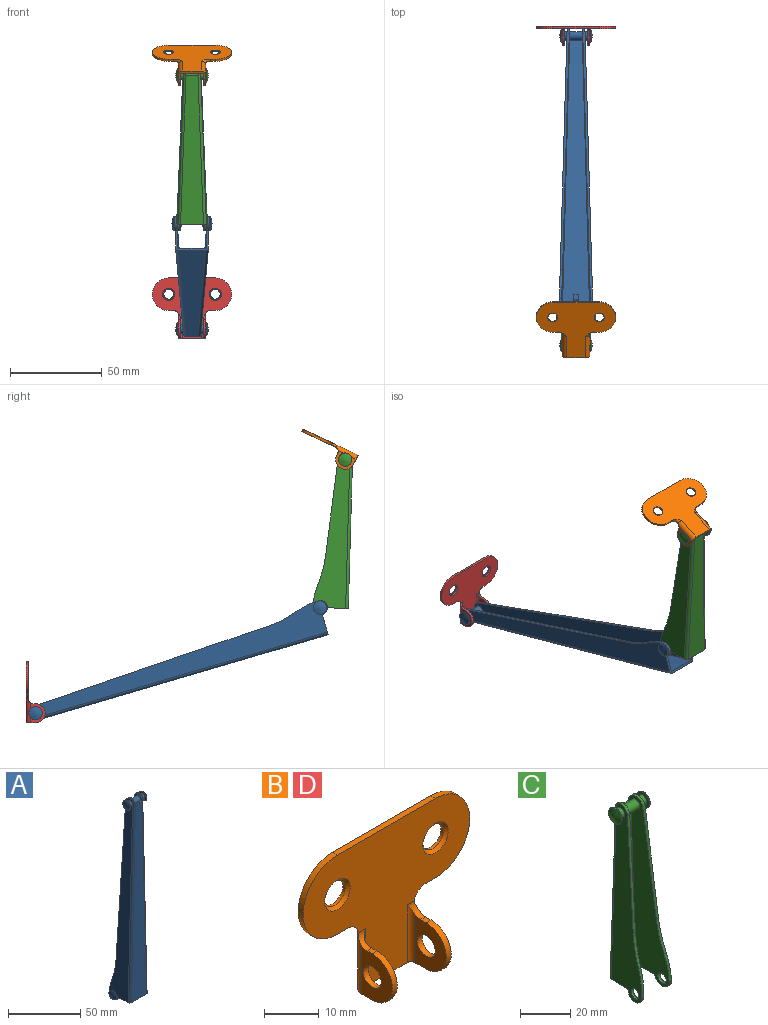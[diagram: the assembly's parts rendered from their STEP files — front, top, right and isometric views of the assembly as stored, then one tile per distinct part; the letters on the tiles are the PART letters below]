
ASSEMBLY  parts=4 mates=4
PART A: 52 faces, bbox 22.4x21.2x174.7 mm
  f0: cylinder r=1.52mm len=168.21mm, axis (0.03,0,1), area 390.4mm2, adj f3,f5,f12,f14,f15,f17
  f1: cylinder r=1.52mm len=168.21mm, axis (0.03,0,-1), area 390.5mm2, adj f4,f5,f12,f13,f15,f16
  f2: plane 165.1x15.3mm, normal (0,1,0), area 1825.2mm2, adj f5,f15,f16,f17,f20,f21,f25,f26
  f3: cylinder r=3.94mm len=7.86mm, axis (-1,0,0), area 12.5mm2, adj f0,f10,f14,f17
  f4: cylinder r=3.94mm len=7.86mm, axis (-1,0,0), area 12.5mm2, adj f1,f11,f13,f16
  f5: plane 18.57x11.45mm, normal (0,0,-1), area 47.5mm2, adj f0,f1,f2,f6,f7,f12,f13,f14
  f6: cylinder r=3.94mm len=7.87mm, axis (-1,0,0), area 15.7mm2, adj f5,f8,f14,f17
  f7: cylinder r=3.94mm len=7.87mm, axis (-1,0,0), area 15.7mm2, adj f5,f9,f13,f16
  f8: cylinder r=35.37mm len=12.06mm, axis (-1,0,0), area 15.6mm2, adj f6,f14,f17,f19
  f9: cylinder r=35.37mm len=12.06mm, axis (-1,0,0), area 15.6mm2, adj f7,f13,f16,f18
  f10: plane 135.82x5.87mm, normal (0,1,0.04), area 172.8mm2, adj f3,f14,f17,f19
  f11: plane 135.82x5.87mm, normal (0,1,0.04), area 172.8mm2, adj f4,f13,f16,f18
  f12: plane 165.1x14.81mm, normal (0,-1,0), area 1749.8mm2, adj f0,f1,f5,f15
  f13: plane 173.37x18.23mm, normal (1,-0.03,0.03), area 1722.3mm2, adj f1,f4,f5,f7,f9,f11,f18,f30
  f14: plane 173.33x18.18mm, normal (-1,-0.03,0.03), area 1722.3mm2, adj f0,f3,f5,f6,f8,f10,f19,f32
  f15: plane 6.88x1.27mm, normal (0,0,1), area 8.7mm2, adj f0,f1,f2,f12,f16,f17
  f16: plane 173.26x19.58mm, normal (-1,0.03,-0.03), area 1758.6mm2, adj f1,f2,f4,f5,f7,f9,f11,f15
  f17: plane 173.37x19.69mm, normal (1,0.03,-0.03), area 1758.6mm2, adj f0,f2,f3,f5,f6,f8,f10,f15
  f18: cylinder r=58.42mm len=17.39mm, axis (-1,0,0), area 22.6mm2, adj f9,f11,f13,f16
  f19: cylinder r=58.42mm len=17.39mm, axis (-1,0,0), area 22.6mm2, adj f8,f10,f14,f17
  f20: plane 2.54x1.14mm, normal (0,-0.71,0.71), area 4.1mm2, adj f2,f24,f25,f26
  f21: plane 2.67x2.67mm, normal (0,0.71,-0.71), area 9.6mm2, adj f2,f22,f25,f26
  f22: plane 3.17x2.54mm, normal (0,1,0), area 8.1mm2, adj f21,f23,f25,f26
  f23: plane 2.54x1.52mm, normal (0,0,1), area 3.9mm2, adj f22,f24,f25,f26
  f24: plane 2.54x2.54mm, normal (0,-1,0), area 6.5mm2, adj f20,f23,f25,f26
  f25: plane 5.84x2.67mm, normal (1,0,0), area 8.5mm2, adj f2,f20,f21,f22,f23,f24
  f26: plane 5.84x2.67mm, normal (-1,0,0), area 8.5mm2, adj f2,f20,f21,f22,f23,f24
  f27: bspline ~7.55x7.44mm, area 43.1mm2, adj f28
  f28: cylinder r=3.64mm len=7.29mm, axis (-1,0,0), area 11.6mm2, adj f27,f29
  f29: plane 7.29x7.29mm, normal (-1,0,0), area 25mm2, adj f28,f30
  f30: cylinder r=2.31mm len=4.62mm, axis (-1,0,0), area 39.5mm2, adj f13,f29
  f31: cylinder r=2.31mm len=7.06mm, axis (-1,0,0), area 101.1mm2, adj f16,f17
  f32: cylinder r=2.31mm len=4.62mm, axis (-1,0,0), area 42.1mm2, adj f14,f33
  f33: plane 7.29x7.29mm, normal (1,0,0), area 25mm2, adj f32,f34
  f34: cylinder r=3.64mm len=7.29mm, axis (1,0,0), area 11.6mm2, adj f33,f35
  f35: bspline ~7.55x7.44mm, area 43.1mm2, adj f34
  f36: bspline ~7.55x7.45mm, area 43.1mm2, adj f37
  f37: cylinder r=3.64mm len=7.29mm, axis (-1,0,0), area 11.6mm2, adj f36,f38
  f38: plane 7.29x7.29mm, normal (-1,0,0), area 25mm2, adj f37,f39
  f39: cylinder r=2.31mm len=4.62mm, axis (-1,0,0), area 3.7mm2, adj f13,f38
  f40: cylinder r=2.31mm len=4.62mm, axis (-1,0,0), area 15.8mm2, adj f16,f41
  f41: plane 7.75x7.75mm, normal (1,-0.03,-0.04), area 24.9mm2, adj f40,f42
  f42: extruded ~7.3x7.29mm, area 11.6mm2, adj f41,f43
  f43: bspline ~10.59x10.59mm, area 43.1mm2, adj f42
  f44: bspline ~7.55x7.45mm, area 43.1mm2, adj f45
  f45: cylinder r=3.64mm len=7.29mm, axis (1,0,0), area 11.6mm2, adj f44,f46
  f46: plane 7.29x7.29mm, normal (1,0,0), area 25mm2, adj f45,f47
  f47: cylinder r=2.31mm len=4.62mm, axis (1,0,0), area 3.7mm2, adj f14,f46
  f48: cylinder r=2.31mm len=4.62mm, axis (1,0,0), area 14.4mm2, adj f17,f49
  f49: plane 7.75x7.75mm, normal (-1,-0.03,-0.04), area 24.9mm2, adj f48,f50
  f50: extruded ~7.3x7.29mm, area 11.6mm2, adj f49,f51
  f51: bspline ~10.59x10.59mm, area 43.1mm2, adj f50
PART B: 30 faces, bbox 43.3x15.4x33.3 mm
  f0: plane 15.24x5.21mm, normal (0,0,-1), area 27mm2, adj f1,f2,f7,f11,f12,f15,f16,f17
  f1: cylinder r=5.21mm len=10.41mm, axis (-1,0,0), area 20.8mm2, adj f0,f3,f15,f20
  f2: cylinder r=5.21mm len=10.41mm, axis (-1,0,0), area 20.8mm2, adj f0,f4,f7,f23
  f3: plane 1.4x1.27mm, normal (0,0,1), area 1.8mm2, adj f1,f5,f15,f20
  f4: plane 1.4x1.27mm, normal (0,0,1), area 1.8mm2, adj f2,f6,f7,f23
  f5: cylinder r=2.54mm len=2.54mm, axis (1,0,0), area 5.5mm2, adj f3,f12,f15,f17,f19,f20,f21
  f6: cylinder r=2.54mm len=2.54mm, axis (1,0,0), area 5.5mm2, adj f4,f7,f12,f16,f18,f22,f23
  f7: plane 10.75x7.87mm, normal (-1,0,0), area 53.7mm2, adj f0,f2,f4,f6,f16,f28
  f8: plane 3.22x1.27mm, normal (0,0,-1), area 3.7mm2, adj f9,f11,f12,f18
  f9: cylinder r=8.89mm len=17.78mm, axis (0,1,0), area 35.5mm2, adj f8,f10,f11,f12
  f10: plane 25.4x1.27mm, normal (0,0,1), area 32.3mm2, adj f9,f11,f12,f14
  f11: plane 43.18x33.15mm, normal (0,1,0), area 819.1mm2, adj f0,f8,f9,f10,f13,f14,f16,f17
  f12: plane 43.3x33.26mm, normal (0,-1,0), area 807.8mm2, adj f0,f5,f6,f8,f9,f10,f13,f14
  f13: plane 3.22x1.27mm, normal (0,0,-1), area 3.7mm2, adj f11,f12,f14,f19
  f14: cylinder r=8.89mm len=17.78mm, axis (0,1,0), area 35.5mm2, adj f10,f11,f12,f13
  f15: plane 10.75x7.87mm, normal (1,0,0), area 53.7mm2, adj f0,f1,f3,f5,f17,f29
  f16: cylinder r=2.54mm len=12.83mm, axis (0,0,-1), area 49.3mm2, adj f0,f6,f7,f11,f18
  f17: cylinder r=2.54mm len=12.83mm, axis (0,0,1), area 49.3mm2, adj f0,f5,f11,f15,f19
  f18: torus R=5.08mm, axis (0,0,-1), area 6.9mm2, adj f6,f8,f11,f12,f16
  f19: torus R=5.08mm, axis (0,0,-1), area 6.9mm2, adj f5,f11,f12,f13,f17
  f20: plane 10.92x8.13mm, normal (-1,0,0), area 56.5mm2, adj f0,f1,f3,f5,f21,f29
  f21: cylinder r=1.02mm len=12.95mm, axis (0,0,-1), area 19.1mm2, adj f0,f5,f12,f20
  f22: cylinder r=1.02mm len=12.95mm, axis (0,0,-1), area 19.1mm2, adj f0,f6,f12,f23
  f23: plane 10.92x8.13mm, normal (1,0,0), area 56.5mm2, adj f0,f2,f4,f6,f22,f28
  f24: cylinder r=2.67mm len=5.33mm, axis (0,-1,0), area 10.6mm2, adj f11,f27
  f25: cylinder r=2.67mm len=5.33mm, axis (0,-1,0), area 10.6mm2, adj f11,f26
  f26: cone r=3.3mm half-angle=45deg, axis (0,-1,0), area 16.8mm2, adj f12,f25
  f27: cone r=3.3mm half-angle=45deg, axis (0,-1,0), area 16.8mm2, adj f12,f24
  f28: cylinder r=2.31mm len=4.62mm, axis (1,0,0), area 18.4mm2, adj f7,f23
  f29: cylinder r=2.31mm len=4.62mm, axis (1,0,0), area 18.4mm2, adj f15,f20
PART C: 38 faces, bbox 18.3x19.8x89.4 mm
  f0: cylinder r=2.31mm len=4.62mm, axis (-1,0,0), area 41.7mm2, adj f1,f18
  f1: plane 7.29x7.29mm, normal (1,0,0), area 25mm2, adj f0,f2
  f2: cylinder r=3.64mm len=7.29mm, axis (1,0,0), area 11.6mm2, adj f1,f3
  f3: bspline ~7.55x7.44mm, area 43.1mm2, adj f2
  f4: cylinder r=1.52mm len=84.15mm, axis (-0.04,0,-1), area 193.7mm2, adj f9,f14,f15,f18,f19,f21
  f5: cylinder r=1.52mm len=84.15mm, axis (-0.04,0,1), area 193.7mm2, adj f11,f14,f15,f16,f19,f20
  f6: plane 81.03x13mm, normal (0,-1,0), area 803.3mm2, adj f14,f19,f20,f21,f29,f30,f31,f32
  f7: cylinder r=35.37mm len=12.81mm, axis (-1,0,0), area 16.7mm2, adj f8,f18,f21,f23
  f8: cylinder r=3.94mm len=7.87mm, axis (-1,0,0), area 15.7mm2, adj f7,f14,f18,f21
  f9: cylinder r=3.94mm len=7.84mm, axis (-1,0,0), area 12mm2, adj f4,f10,f18,f21
  f10: plane 53.31x5.38mm, normal (0,-0.99,0.1), area 68.1mm2, adj f9,f18,f21,f23
  f11: plane 89.37x18.31mm, normal (1,0.03,0.04), area 915mm2, adj f5,f12,f13,f14,f16,f17,f22,f25
  f12: cylinder r=35.37mm len=12.81mm, axis (-1,0,0), area 16.7mm2, adj f11,f13,f20,f22
  f13: cylinder r=3.94mm len=7.87mm, axis (-1,0,0), area 15.7mm2, adj f11,f12,f14,f20
  f14: plane 16.27x11.45mm, normal (0,0,-1), area 44.6mm2, adj f4,f5,f6,f8,f11,f13,f15,f18
  f15: plane 81.03x12.51mm, normal (0,1,0), area 769.1mm2, adj f4,f5,f14,f19
  f16: cylinder r=3.94mm len=7.84mm, axis (-1,0,0), area 12mm2, adj f5,f11,f17,f20
  f17: plane 53.31x5.38mm, normal (0,-0.99,0.1), area 68.1mm2, adj f11,f16,f20,f22
  f18: plane 89.37x18.31mm, normal (-1,0.03,0.04), area 915mm2, adj f0,f4,f7,f8,f9,f10,f14,f23
  f19: plane 6.97x1.28mm, normal (0,0,1), area 8.8mm2, adj f4,f5,f6,f15,f20,f21
  f20: plane 89.37x19.76mm, normal (-1,-0.03,-0.04), area 934.5mm2, adj f5,f6,f12,f13,f14,f16,f17,f19
  f21: plane 89.37x19.76mm, normal (1,-0.03,-0.04), area 934.5mm2, adj f4,f6,f7,f8,f9,f10,f14,f19
  f22: cylinder r=58.42mm len=15.3mm, axis (-1,0,0), area 20.1mm2, adj f11,f12,f17,f20
  f23: cylinder r=58.42mm len=15.3mm, axis (-1,0,0), area 20.1mm2, adj f7,f10,f18,f21
  f24: cylinder r=2.31mm len=4.62mm, axis (1,0,0), area 18.5mm2, adj f18,f21
  f25: cylinder r=2.31mm len=4.62mm, axis (1,0,0), area 18.5mm2, adj f11,f20
  f26: plane 2.54x2.54mm, normal (0,1,0), area 6.5mm2, adj f27,f30,f31,f32
  f27: plane 2.54x1.52mm, normal (0,0,1), area 3.9mm2, adj f26,f28,f31,f32
  f28: plane 3.17x2.54mm, normal (0,-1,0), area 8.1mm2, adj f27,f29,f31,f32
  f29: plane 2.67x2.67mm, normal (0,-0.71,-0.71), area 9.6mm2, adj f6,f28,f31,f32
  f30: plane 2.54x1.14mm, normal (0,0.71,0.71), area 4.1mm2, adj f6,f26,f31,f32
  f31: plane 5.84x2.67mm, normal (1,0,0), area 8.5mm2, adj f6,f26,f27,f28,f29,f30
  f32: plane 5.84x2.67mm, normal (-1,0,0), area 8.5mm2, adj f6,f26,f27,f28,f29,f30
  f33: cylinder r=2.31mm len=7.15mm, axis (-1,0,0), area 102.2mm2, adj f20,f21
  f34: bspline ~7.55x7.44mm, area 43.1mm2, adj f35
  f35: cylinder r=3.64mm len=7.29mm, axis (-1,0,0), area 11.6mm2, adj f34,f36
  f36: plane 7.29x7.29mm, normal (-1,0,0), area 25mm2, adj f35,f37
  f37: cylinder r=2.31mm len=4.62mm, axis (-1,0,0), area 38.5mm2, adj f11,f36
PART D: same geometry as B
PLACE A rot(axis=(0,-0.8,-0.6),180deg) t=(0,-160.37,41.77)mm
PLACE B rot(axis=(0,-0.54,-0.84),180deg) t=(0,-242.59,77.69)mm
PLACE C rot(axis=(0,0.01,-1),180deg) t=(0,-160.37,41.77)mm
PLACE D rot(axis=(-1,0,0),0deg) t=(0,-16.64,-96.83)mm
MATE planar B.f1 <-> D.f1  axis (1,0,0) through (-6.35,-174.08,122.44)mm
MATE revolute D.f1 <-> A.f3  axis (-1,0,0) through (-7.62,-5.21,-15.8)mm
MATE cylindrical C.f8 <-> A.f37  axis (-1,0,0) through (-8.39,-160.37,41.77)mm
MATE revolute C.f0 <-> B.f1  axis (1,0,0) through (-7.62,-174.08,122.44)mm
